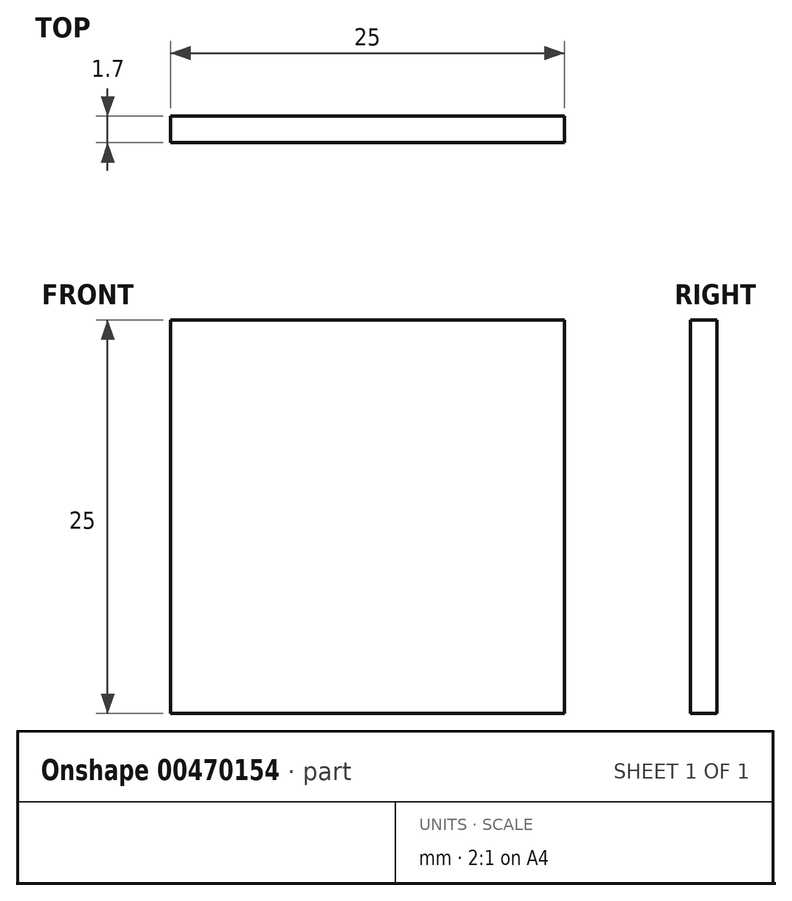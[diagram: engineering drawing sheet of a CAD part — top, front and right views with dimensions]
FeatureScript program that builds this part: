
annotation { "Feature Type Name" : "Feature", "Feature Type Description" : "" }
export const myFeature = defineFeature(function(context is Context, id is Id, definition is map)
    precondition{}
    {
        {
            var Q0;
            Q0=qCreatedBy(makeId("Front.planeOp"),FACE);
            var sketch = newSketch(context, id + "F0", { "sketchPlane" : qUnion([Q0])});
            skLineSegment(sketch, "E0.bottom", {"start": v(-25, 25) * mm, "end": v(25, 25) * mm});
            skLineSegment(sketch, "E0.top", {"start": v(-25, -25) * mm, "end": v(25, -25) * mm});
            skLineSegment(sketch, "E0.left", {"start": v(-25, 25) * mm, "end": v(-25, -25) * mm});
            skLineSegment(sketch, "E0.right", {"start": v(25, 25) * mm, "end": v(25, -25) * mm});
            skPoint(sketch, "E0.middle", {"position": v(0, 0) * mm});
            skLineSegment(sketch, "E1.bottom", {"start": v(-12.5, 12.5) * mm, "end": v(12.5, 12.5) * mm});
            skLineSegment(sketch, "E1.top", {"start": v(-12.5, -12.5) * mm, "end": v(12.5, -12.5) * mm});
            skLineSegment(sketch, "E1.left", {"start": v(-12.5, 12.5) * mm, "end": v(-12.5, -12.5) * mm});
            skLineSegment(sketch, "E1.right", {"start": v(12.5, 12.5) * mm, "end": v(12.5, -12.5) * mm});
            skSolve(sketch);
        }
        {
            var Q0;
            Q0=makeQuery(id+"F0.imprint","IMPRINT",FACE,{"disambiguationData":[TD([[makeQuery(id+"F0.imprint","IMPRINT",EDGE,{"derivedFrom":sQuery(id+"F0.wireOp",EDGE,"E1.bottom")}),-1.0]])]});
            extrude(context, id + "F1", {"entities" : qUnion([Q0]), "depth" : 1.7 * mm});
        }
    });
